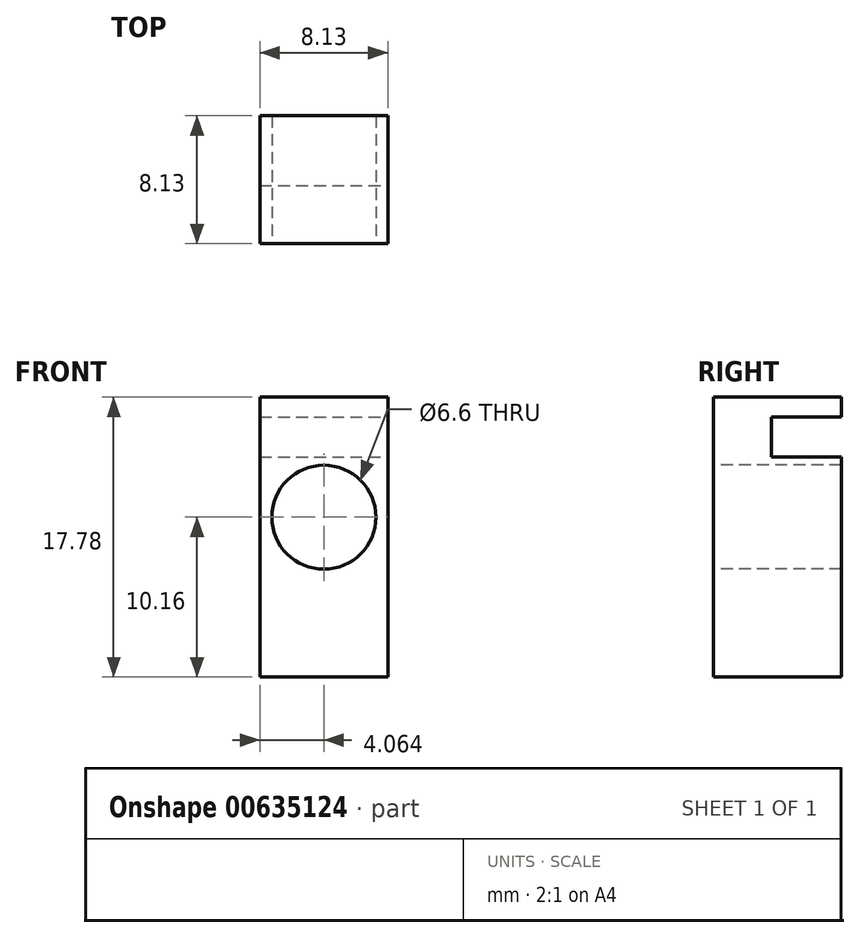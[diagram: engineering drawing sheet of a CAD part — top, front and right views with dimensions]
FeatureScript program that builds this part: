
annotation { "Feature Type Name" : "Feature", "Feature Type Description" : "" }
export const myFeature = defineFeature(function(context is Context, id is Id, definition is map)
    precondition{}
    {
        {
            var Q0;
            Q0=qCreatedBy(makeId("Top.planeOp"),FACE);
            var sketch = newSketch(context, id + "F0", { "sketchPlane" : qUnion([Q0])});
            skLineSegment(sketch, "E0.bottom", {"start": v(0, 0) * mm, "end": v(8.13, 0) * mm});
            skLineSegment(sketch, "E0.top", {"start": v(0, 8.13) * mm, "end": v(8.13, 8.13) * mm});
            skLineSegment(sketch, "E0.left", {"start": v(0, 0) * mm, "end": v(0, 8.13) * mm});
            skLineSegment(sketch, "E0.right", {"start": v(8.13, 0) * mm, "end": v(8.13, 8.13) * mm});
            skSolve(sketch);
        }
        {
            var Q0;
            Q0 = qSketchRegion(id + "F0", true);
            extrude(context, id + "F1", {"entities" : qUnion([Q0]), "depth" : 17.78 * mm, "offsetDistance" : 25.4 * mm});
        }
        {
            var Q0;
            Q0=makeQuery(id+"F1.opExtrude","SWEPT_FACE",FACE,{"disambiguationData":[OSD([sQuery(id+"F0.wireOp",EDGE,"E0.right")])]});
            var sketch = newSketch(context, id + "F2", { "sketchPlane" : qUnion([Q0])});
            skLineSegment(sketch, "E1", {"start": v(8.13, 13.97) * mm, "end": v(8.13, 17.78) * mm});
            skLineSegment(sketch, "E2", {"start": v(8.13, 13.97) * mm, "end": v(8.13, 0) * mm});
            skLineSegment(sketch, "E3.bottom", {"start": v(8.13, 16.51) * mm, "end": v(3.68, 16.51) * mm});
            skLineSegment(sketch, "E3.top", {"start": v(8.13, 13.97) * mm, "end": v(3.68, 13.97) * mm});
            skLineSegment(sketch, "E3.left", {"start": v(8.13, 16.51) * mm, "end": v(8.13, 13.97) * mm});
            skLineSegment(sketch, "E3.right", {"start": v(3.68, 16.51) * mm, "end": v(3.68, 13.97) * mm});
            skSolve(sketch);
        }
        {
            var Q0;
            Q0=makeQuery(id+"F2.imprint","IMPRINT",FACE,{"disambiguationData":[TD([[makeQuery(id+"F2.imprint","IMPRINT",EDGE,{"derivedFrom":sQuery(id+"F2.wireOp",EDGE,"E3.bottom")}),1.0]])]});
            extrude(context, id + "F3", {"entities" : qUnion([Q0]), "operationType" : NewBodyOperationType.REMOVE, "oppositeDirection" : true, "depth" : 25.4 * mm, "offsetDistance" : 25.4 * mm});
        }
        {
            var Q0;
            Q0=makeQuery(id+"F1.opExtrude","SWEPT_FACE",FACE,{"disambiguationData":[OSD([sQuery(id+"F0.wireOp",EDGE,"E0.bottom")])]});
            var sketch = newSketch(context, id + "F4", { "sketchPlane" : qUnion([Q0])});
            skCircle(sketch, "E4", {"center": v(4.06, 10.16) * mm, "radius": 3.3 * mm});
            skPoint(sketch, "E4.centerSnap0", {"position": v(4.06, 0) * mm});
            skSolve(sketch);
        }
        {
            var Q0;
            Q0=makeQuery(id+"F4.imprint","IMPRINT",FACE,{"disambiguationData":[TD([[makeQuery(id+"F4.imprint","IMPRINT",EDGE,{"derivedFrom":sQuery(id+"F4.wireOp",EDGE,"E4")}),1.0]])]});
            extrude(context, id + "F5", {"entities" : qUnion([Q0]), "operationType" : NewBodyOperationType.REMOVE, "oppositeDirection" : true, "depth" : 25.4 * mm, "offsetDistance" : 25.4 * mm});
        }
    });
